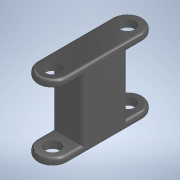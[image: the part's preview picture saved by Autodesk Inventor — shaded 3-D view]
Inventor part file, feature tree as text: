
AUTODESK INVENTOR PART (.ipt)
format: ipt  version: 2022 (Build 260153000, 153)  size: 169,472 bytes
history: native  units: mm (DEFAULTED — no unit token found)
features: extrude x2, sketch x2, mirror x1, fillet x1
ambient origin geometry x8: Origin, YZ Plane, XZ Plane, XY Plane, X Axis, Y Axis, Z Axis, Center Point
bodies: Solid1 (feature_tree)
feature tree (6):
  extrude  "Extrusion1"  Depth=40.0mm
  extrude  "Extrusion2"  Depth=2.0mm
  mirror  "Mirror1"
  fillet  "Fillet1"  [1 undecoded]
  sketch  "Sketch1"  dims[d4=50.0mm d5=0.0mm d6=40.0mm]
  sketch  "Sketch2"  dims[d7=50.0mm d8=0.0mm d9=2.0mm]
note: 1 required parameter value undecoded (feature->parameter linkage not recoverable at this tier; creation-order binding heuristic only, values carry confidence <= 0.55)
